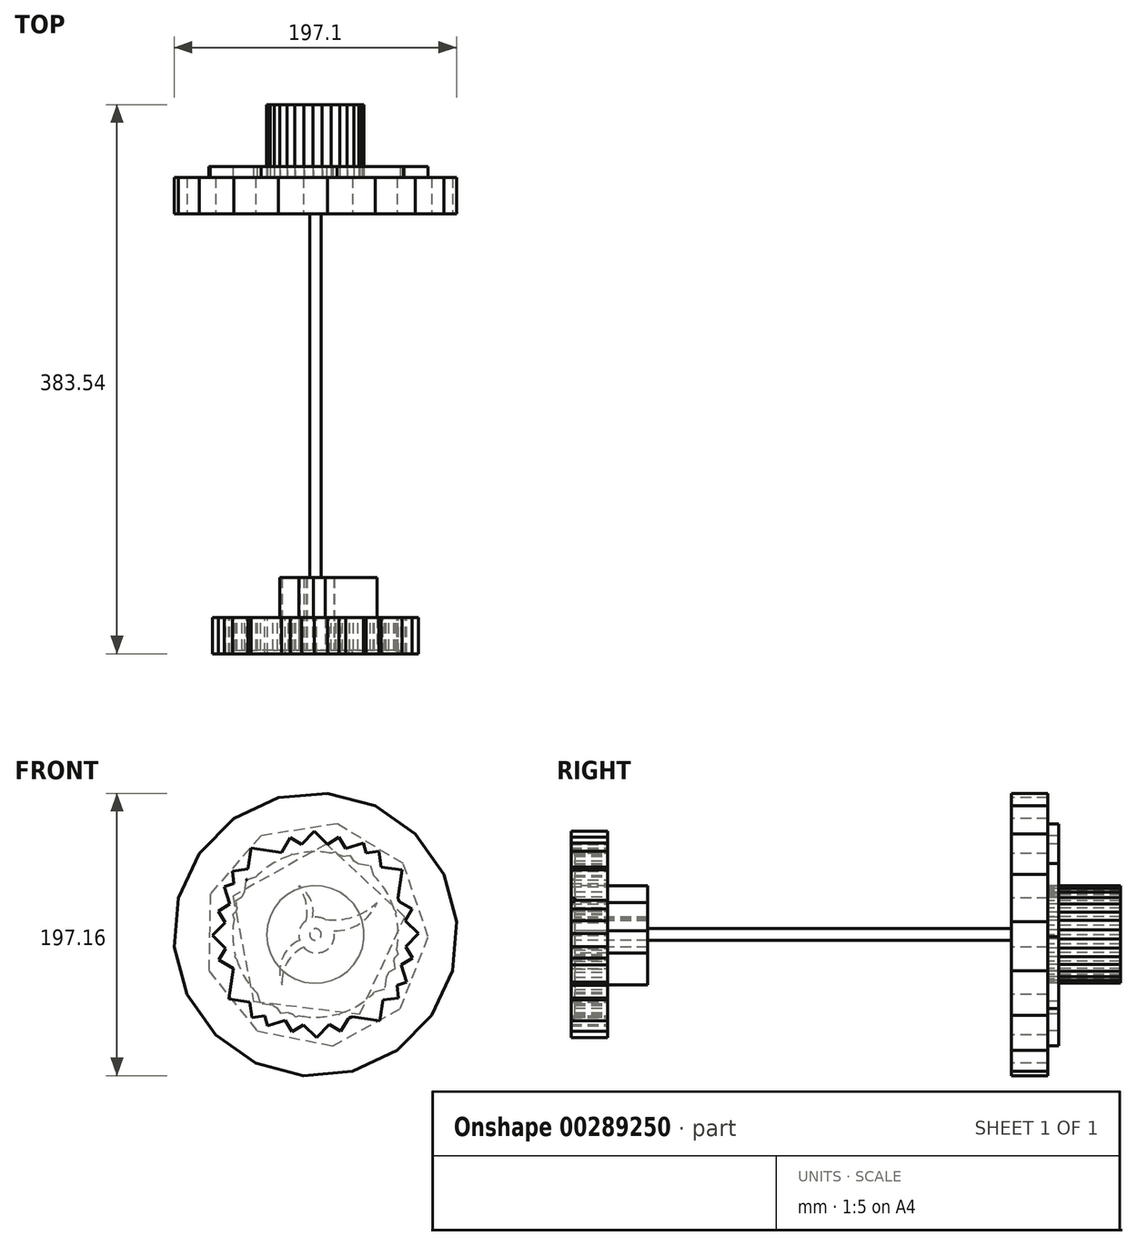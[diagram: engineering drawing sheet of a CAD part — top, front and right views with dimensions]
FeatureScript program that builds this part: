
annotation { "Feature Type Name" : "Feature", "Feature Type Description" : "" }
export const myFeature = defineFeature(function(context is Context, id is Id, definition is map)
    precondition{}
    {
        {
            var Q0;
            Q0=qCreatedBy(makeId("Front.planeOp"),FACE);
            var sketch = newSketch(context, id + "F0", { "sketchPlane" : qUnion([Q0])});
            skCircle(sketch, "E0", {"center": v(0, 0) * mm, "radius": 57.78 * mm});
            skCircle(sketch, "E1.cCircle", {"center": v(0, 0) * mm, "radius": 49.37 * mm, "construction": true});
            skLineSegment(sketch, "E1.0", {"start": v(-67.54, -17.7) * mm, "end": v(-17.7, 67.54) * mm});
            skLineSegment(sketch, "E1.1", {"start": v(-17.7, 67.54) * mm, "end": v(67.54, 17.7) * mm});
            skLineSegment(sketch, "E1.2", {"start": v(67.54, 17.7) * mm, "end": v(17.7, -67.54) * mm});
            skLineSegment(sketch, "E1.3", {"start": v(17.7, -67.54) * mm, "end": v(-67.54, -17.7) * mm});
            skPoint(sketch, "E1.0.midPoint", {"position": v(-42.62, 24.92) * mm});
            skLineSegment(sketch, "E2.0", {"start": v(-67.9, 16.32) * mm, "end": v(16.32, 67.9) * mm});
            skLineSegment(sketch, "E2.1", {"start": v(16.32, 67.9) * mm, "end": v(67.9, -16.32) * mm});
            skLineSegment(sketch, "E2.2", {"start": v(67.9, -16.32) * mm, "end": v(-16.32, -67.9) * mm});
            skLineSegment(sketch, "E2.3", {"start": v(-16.32, -67.9) * mm, "end": v(-67.9, 16.32) * mm});
            skPoint(sketch, "E2.0.midPoint", {"position": v(-25.78, 42.1) * mm});
            skCircle(sketch, "E3.cCircle", {"center": v(0, 0) * mm, "radius": 53.26 * mm, "construction": true});
            skLineSegment(sketch, "E3.0", {"start": v(-45.03, 60.38) * mm, "end": v(60.38, 45.03) * mm});
            skLineSegment(sketch, "E3.1", {"start": v(60.38, 45.03) * mm, "end": v(45.03, -60.38) * mm});
            skLineSegment(sketch, "E3.2", {"start": v(45.03, -60.38) * mm, "end": v(-60.38, -45.03) * mm});
            skLineSegment(sketch, "E3.3", {"start": v(-60.38, -45.03) * mm, "end": v(-45.03, 60.38) * mm});
            skPoint(sketch, "E3.0.midPoint", {"position": v(7.67, 52.7) * mm});
            skCircle(sketch, "E4.cCircle", {"center": v(0, 0) * mm, "radius": 50.9 * mm, "construction": true});
            skLineSegment(sketch, "E4.0", {"start": v(-72, -0.73) * mm, "end": v(-0.73, 72) * mm});
            skLineSegment(sketch, "E4.1", {"start": v(-0.73, 72) * mm, "end": v(72, 0.73) * mm});
            skLineSegment(sketch, "E4.2", {"start": v(72, 0.73) * mm, "end": v(0.73, -72) * mm});
            skLineSegment(sketch, "E4.3", {"start": v(0.73, -72) * mm, "end": v(-72, -0.73) * mm});
            skPoint(sketch, "E4.0.midPoint", {"position": v(-36.36, 35.63) * mm});
            skLineSegment(sketch, "E5.0", {"start": v(-63.79, 33.38) * mm, "end": v(33.38, 63.79) * mm});
            skLineSegment(sketch, "E5.1", {"start": v(33.38, 63.79) * mm, "end": v(63.79, -33.38) * mm});
            skLineSegment(sketch, "E5.2", {"start": v(63.79, -33.38) * mm, "end": v(-33.38, -63.79) * mm});
            skLineSegment(sketch, "E5.3", {"start": v(-33.38, -63.79) * mm, "end": v(-63.79, 33.38) * mm});
            skPoint(sketch, "E5.0.midPoint", {"position": v(-15.2, 48.59) * mm});
            skCircle(sketch, "E6.cCircle", {"center": v(0, 0) * mm, "radius": 51.65 * mm, "construction": true});
            skLineSegment(sketch, "E6.0", {"start": v(-58.08, 44.3) * mm, "end": v(44.3, 58.08) * mm});
            skLineSegment(sketch, "E6.1", {"start": v(44.3, 58.08) * mm, "end": v(58.08, -44.3) * mm});
            skLineSegment(sketch, "E6.2", {"start": v(58.08, -44.3) * mm, "end": v(-44.3, -58.08) * mm});
            skLineSegment(sketch, "E6.3", {"start": v(-44.3, -58.08) * mm, "end": v(-58.08, 44.3) * mm});
            skPoint(sketch, "E6.0.midPoint", {"position": v(-6.9, 51.19) * mm});
            skSolve(sketch);
        }
        {
            var Q0;
            Q0 = qSketchRegion(id + "F0", true);
            extrude(context, id + "F1", {"entities" : qUnion([Q0]), "depth" : 25.4 * mm});
        }
        {
            var Q0;
            Q0=makeQuery(id+"F1.opExtrude","CAP_FACE",FACE,{"disambiguationData":[OSD([sQuery(id+"F0.wireOp",EDGE,"E0"),sQuery(id+"F0.wireOp",EDGE,"E1.0"),sQuery(id+"F0.wireOp",EDGE,"E1.1"),sQuery(id+"F0.wireOp",EDGE,"E1.2"),sQuery(id+"F0.wireOp",EDGE,"E1.3"),sQuery(id+"F0.wireOp",EDGE,"E2.0"),sQuery(id+"F0.wireOp",EDGE,"E2.1"),sQuery(id+"F0.wireOp",EDGE,"E2.2"),sQuery(id+"F0.wireOp",EDGE,"E2.3"),sQuery(id+"F0.wireOp",EDGE,"E3.0"),sQuery(id+"F0.wireOp",EDGE,"E3.1"),sQuery(id+"F0.wireOp",EDGE,"E3.2"),sQuery(id+"F0.wireOp",EDGE,"E3.3"),sQuery(id+"F0.wireOp",EDGE,"E4.0"),sQuery(id+"F0.wireOp",EDGE,"E4.1"),sQuery(id+"F0.wireOp",EDGE,"E4.2"),sQuery(id+"F0.wireOp",EDGE,"E4.3"),sQuery(id+"F0.wireOp",EDGE,"E5.0"),sQuery(id+"F0.wireOp",EDGE,"E5.1"),sQuery(id+"F0.wireOp",EDGE,"E5.2"),sQuery(id+"F0.wireOp",EDGE,"E5.3"),sQuery(id+"F0.wireOp",EDGE,"E6.0"),sQuery(id+"F0.wireOp",EDGE,"E6.1"),sQuery(id+"F0.wireOp",EDGE,"E6.2"),sQuery(id+"F0.wireOp",EDGE,"E6.3")])],"isStart":false});
            var sketch = newSketch(context, id + "F2", { "sketchPlane" : qUnion([Q0])});
            skCircle(sketch, "E7", {"center": v(0.85, -0.42) * mm, "radius": 62.29 * mm});
            skSolve(sketch);
        }
        {
            var Q0;
            Q0 = qSketchRegion(id + "F2", true);
            extrude(context, id + "F3", {"entities" : qUnion([Q0]), "operationType" : NewBodyOperationType.ADD, "oppositeDirection" : true, "depth" : 2.54 * mm});
        }
        {
            var Q0;
            {var subQ1=sQuery(id+"F0.wireOp",EDGE,"E0");var subQ14=sQuery(id+"F0.wireOp",EDGE,"E3.0");var subQ75=makeQuery(id+"F0.imprint","INTERSECT",VERTEX,{"disambiguationData":[OD(0.0)],"derivedFrom":[subQ1,subQ14]});var subQ89=sQuery(id+"F2.wireOp",EDGE,"E7");Q0=makeQuery(id+"F3.boolean.opBoolean","SPLIT",FACE,{"disambiguationData":[TD([makeQuery(id+"F1.opExtrude","SWEPT_FACE",FACE,{"disambiguationData":[OSD([subQ1]),TDD([makeQuery(id+"F0.imprint","IMPRINT",EDGE,{"disambiguationData":[TD([[subQ75,-1.0]])],"derivedFrom":subQ1})])]})])],"derivedFrom":makeQuery(id+"F3.opExtrude","CAP_FACE",FACE,{"disambiguationData":[OSD([subQ89])],"isStart":false})});}
            var sketch = newSketch(context, id + "F4", { "sketchPlane" : qUnion([Q0])});
            skCircle(sketch, "E8", {"center": v(-0.85, -0.42) * mm, "radius": 12.46 * mm});
            skArc(sketch, "E9", {"start": v(-42.97, 22.23) * mm, "mid": v(-31.02, 7.72) * mm, "end": v(-12.93, 2.62) * mm});
            skArc(sketch, "E10", {"start": v(-42.97, 22.23) * mm, "mid": v(-26.23, 12.24) * mm, "end": v(-6.81, 10.52) * mm});
            skArc(sketch, "E11", {"start": v(23.28, -35.14) * mm, "mid": v(23.38, -17.14) * mm, "end": v(11.1, -3.98) * mm});
            skArc(sketch, "E12", {"start": v(23.28, -35.14) * mm, "mid": v(19.84, -19.7) * mm, "end": v(8.2, -9) * mm});
            skArc(sketch, "E13", {"start": v(11.64, 33.87) * mm, "mid": v(3.34, 24.3) * mm, "end": v(1.97, 11.72) * mm});
            skArc(sketch, "E14", {"start": v(11.64, 33.87) * mm, "mid": v(6.6, 22.3) * mm, "end": v(6.46, 9.67) * mm});
            skArc(sketch, "E15", {"start": v(-20.1, -29.85) * mm, "mid": v(-8, -25.09) * mm, "end": v(-3.39, -12.91) * mm});
            skArc(sketch, "E16", {"start": v(-20.1, -29.85) * mm, "mid": v(-12.7, -20.27) * mm, "end": v(-10.44, -8.37) * mm});
            skSolve(sketch);
        }
        {
            var Q0;
            Q0 = qSketchRegion(id + "F4", true);
            extrude(context, id + "F5", {"entities" : qUnion([Q0]), "operationType" : NewBodyOperationType.ADD, "depth" : 50.8 * mm});
        }
        {
            var Q0;
            Q0=makeQuery(id+"F5.opExtrude","CAP_FACE",FACE,{"disambiguationData":[OSD([sQuery(id+"F4.wireOp",EDGE,"E8"),sQuery(id+"F4.wireOp",EDGE,"E9"),sQuery(id+"F4.wireOp",EDGE,"E10"),sQuery(id+"F4.wireOp",EDGE,"E11"),sQuery(id+"F4.wireOp",EDGE,"E12"),sQuery(id+"F4.wireOp",EDGE,"E13"),sQuery(id+"F4.wireOp",EDGE,"E14")])],"isStart":false});
            var sketch = newSketch(context, id + "F6", { "sketchPlane" : qUnion([Q0])});
            skCircle(sketch, "E17", {"center": v(0, 0) * mm, "radius": 4.04 * mm});
            skSolve(sketch);
        }
        {
            var Q0;
            Q0 = qSketchRegion(id + "F6", true);
            extrude(context, id + "F7", {"entities" : qUnion([Q0]), "operationType" : NewBodyOperationType.ADD, "depth" : 254 * mm});
        }
        {
            var Q0;
            Q0=makeQuery(id+"F7.opExtrude","CAP_FACE",FACE,{"disambiguationData":[OSD([sQuery(id+"F6.wireOp",EDGE,"E17")])],"isStart":false});
            var sketch = newSketch(context, id + "F8", { "sketchPlane" : qUnion([Q0])});
            skCircle(sketch, "E18.cCircle", {"center": v(0, 0) * mm, "radius": 97.44 * mm, "construction": true});
            skLineSegment(sketch, "E18.0", {"start": v(-41.64, 89.75) * mm, "end": v(-8.43, 98.58) * mm});
            skLineSegment(sketch, "E18.1", {"start": v(-8.43, 98.58) * mm, "end": v(25.8, 95.52) * mm});
            skLineSegment(sketch, "E18.2", {"start": v(25.8, 95.52) * mm, "end": v(56.9, 80.94) * mm});
            skLineSegment(sketch, "E18.3", {"start": v(56.9, 80.94) * mm, "end": v(81.16, 56.6) * mm});
            skLineSegment(sketch, "E18.4", {"start": v(81.16, 56.6) * mm, "end": v(95.62, 25.42) * mm});
            skLineSegment(sketch, "E18.5", {"start": v(95.62, 25.42) * mm, "end": v(98.55, -8.82) * mm});
            skLineSegment(sketch, "E18.6", {"start": v(98.55, -8.82) * mm, "end": v(89.59, -41.99) * mm});
            skLineSegment(sketch, "E18.7", {"start": v(89.59, -41.99) * mm, "end": v(69.83, -70.1) * mm});
            skLineSegment(sketch, "E18.8", {"start": v(69.83, -70.1) * mm, "end": v(41.64, -89.75) * mm});
            skLineSegment(sketch, "E18.9", {"start": v(41.64, -89.75) * mm, "end": v(8.43, -98.58) * mm});
            skLineSegment(sketch, "E18.10", {"start": v(8.43, -98.58) * mm, "end": v(-25.8, -95.52) * mm});
            skLineSegment(sketch, "E18.11", {"start": v(-25.8, -95.52) * mm, "end": v(-56.9, -80.94) * mm});
            skLineSegment(sketch, "E18.12", {"start": v(-56.9, -80.94) * mm, "end": v(-81.16, -56.6) * mm});
            skLineSegment(sketch, "E18.13", {"start": v(-81.16, -56.6) * mm, "end": v(-95.62, -25.42) * mm});
            skLineSegment(sketch, "E18.14", {"start": v(-95.62, -25.42) * mm, "end": v(-98.55, 8.82) * mm});
            skLineSegment(sketch, "E18.15", {"start": v(-98.55, 8.82) * mm, "end": v(-89.59, 41.99) * mm});
            skLineSegment(sketch, "E18.16", {"start": v(-89.59, 41.99) * mm, "end": v(-69.83, 70.1) * mm});
            skLineSegment(sketch, "E18.17", {"start": v(-69.83, 70.1) * mm, "end": v(-41.64, 89.75) * mm});
            skPoint(sketch, "E18.0.midPoint", {"position": v(-25.04, 94.17) * mm});
            skSolve(sketch);
        }
        {
            var Q0;
            Q0 = qSketchRegion(id + "F8", true);
            extrude(context, id + "F9", {"entities" : qUnion([Q0]), "operationType" : NewBodyOperationType.ADD, "depth" : 25.4 * mm});
        }
        {
            var Q0;
            Q0=makeQuery(id+"F9.opExtrude","CAP_FACE",FACE,{"disambiguationData":[OSD([sQuery(id+"F8.wireOp",EDGE,"E18.0"),sQuery(id+"F8.wireOp",EDGE,"E18.1"),sQuery(id+"F8.wireOp",EDGE,"E18.2"),sQuery(id+"F8.wireOp",EDGE,"E18.3"),sQuery(id+"F8.wireOp",EDGE,"E18.4"),sQuery(id+"F8.wireOp",EDGE,"E18.5"),sQuery(id+"F8.wireOp",EDGE,"E18.6"),sQuery(id+"F8.wireOp",EDGE,"E18.7"),sQuery(id+"F8.wireOp",EDGE,"E18.8"),sQuery(id+"F8.wireOp",EDGE,"E18.9"),sQuery(id+"F8.wireOp",EDGE,"E18.10"),sQuery(id+"F8.wireOp",EDGE,"E18.11"),sQuery(id+"F8.wireOp",EDGE,"E18.12"),sQuery(id+"F8.wireOp",EDGE,"E18.13"),sQuery(id+"F8.wireOp",EDGE,"E18.14"),sQuery(id+"F8.wireOp",EDGE,"E18.15"),sQuery(id+"F8.wireOp",EDGE,"E18.16"),sQuery(id+"F8.wireOp",EDGE,"E18.17")])],"isStart":false});
            var sketch = newSketch(context, id + "F10", { "sketchPlane" : qUnion([Q0])});
            skCircle(sketch, "E19.cCircle", {"center": v(0, 0) * mm, "radius": 74 * mm, "construction": true});
            skLineSegment(sketch, "E19.0", {"start": v(-59.3, -51.8) * mm, "end": v(-78.74, -1.56) * mm});
            skLineSegment(sketch, "E19.1", {"start": v(-78.74, -1.56) * mm, "end": v(-61.32, 49.41) * mm});
            skLineSegment(sketch, "E19.2", {"start": v(-61.32, 49.41) * mm, "end": v(-15.21, 77.27) * mm});
            skLineSegment(sketch, "E19.3", {"start": v(-15.21, 77.27) * mm, "end": v(38.01, 68.97) * mm});
            skLineSegment(sketch, "E19.4", {"start": v(38.01, 68.97) * mm, "end": v(73.45, 28.4) * mm});
            skLineSegment(sketch, "E19.5", {"start": v(73.45, 28.4) * mm, "end": v(74.52, -25.46) * mm});
            skLineSegment(sketch, "E19.6", {"start": v(74.52, -25.46) * mm, "end": v(40.72, -67.4) * mm});
            skLineSegment(sketch, "E19.7", {"start": v(40.72, -67.4) * mm, "end": v(-12.13, -77.81) * mm});
            skLineSegment(sketch, "E19.8", {"start": v(-12.13, -77.81) * mm, "end": v(-59.3, -51.8) * mm});
            skPoint(sketch, "E19.0.midPoint", {"position": v(-69.02, -26.69) * mm});
            skCircle(sketch, "E20.cCircle", {"center": v(0, 0) * mm, "radius": 51.46 * mm, "construction": true});
            skLineSegment(sketch, "E20.0", {"start": v(-30.95, -55.58) * mm, "end": v(-62.42, 12.26) * mm});
            skLineSegment(sketch, "E20.1", {"start": v(-62.42, 12.26) * mm, "end": v(-7.63, 63.15) * mm});
            skLineSegment(sketch, "E20.2", {"start": v(-7.63, 63.15) * mm, "end": v(57.7, 26.77) * mm});
            skLineSegment(sketch, "E20.3", {"start": v(57.7, 26.77) * mm, "end": v(43.3, -46.6) * mm});
            skLineSegment(sketch, "E20.4", {"start": v(43.3, -46.6) * mm, "end": v(-30.95, -55.58) * mm});
            skPoint(sketch, "E20.0.midPoint", {"position": v(-46.68, -21.66) * mm});
            skCircle(sketch, "E21.cCircle", {"center": v(0, 0) * mm, "radius": 20.55 * mm, "construction": true});
            skLineSegment(sketch, "E21.0", {"start": v(-20.55, -35.6) * mm, "end": v(-20.55, 35.6) * mm});
            skLineSegment(sketch, "E21.1", {"start": v(-20.55, 35.6) * mm, "end": v(41.1, 0) * mm});
            skLineSegment(sketch, "E21.2", {"start": v(41.1, 0) * mm, "end": v(-20.55, -35.6) * mm});
            skPoint(sketch, "E21.0.midPoint", {"position": v(-20.55, 0) * mm});
            skCircle(sketch, "E22.cCircle", {"center": v(0, 0) * mm, "radius": 7.21 * mm, "construction": true});
            skLineSegment(sketch, "E22.0", {"start": v(-7.21, -1.43) * mm, "end": v(-7.21, 1.43) * mm});
            skLineSegment(sketch, "E22.1", {"start": v(-7.21, 1.43) * mm, "end": v(-6.11, 4.08) * mm});
            skLineSegment(sketch, "E22.2", {"start": v(-6.11, 4.08) * mm, "end": v(-4.08, 6.11) * mm});
            skLineSegment(sketch, "E22.3", {"start": v(-4.08, 6.11) * mm, "end": v(-1.43, 7.21) * mm});
            skLineSegment(sketch, "E22.4", {"start": v(-1.43, 7.21) * mm, "end": v(1.43, 7.21) * mm});
            skLineSegment(sketch, "E22.5", {"start": v(1.43, 7.21) * mm, "end": v(4.08, 6.11) * mm});
            skLineSegment(sketch, "E22.6", {"start": v(4.08, 6.11) * mm, "end": v(6.11, 4.08) * mm});
            skLineSegment(sketch, "E22.7", {"start": v(6.11, 4.08) * mm, "end": v(7.21, 1.43) * mm});
            skLineSegment(sketch, "E22.8", {"start": v(7.21, 1.43) * mm, "end": v(7.21, -1.43) * mm});
            skLineSegment(sketch, "E22.9", {"start": v(7.21, -1.43) * mm, "end": v(6.11, -4.08) * mm});
            skLineSegment(sketch, "E22.10", {"start": v(6.11, -4.08) * mm, "end": v(4.08, -6.11) * mm});
            skLineSegment(sketch, "E22.11", {"start": v(4.08, -6.11) * mm, "end": v(1.43, -7.21) * mm});
            skLineSegment(sketch, "E22.12", {"start": v(1.43, -7.21) * mm, "end": v(-1.43, -7.21) * mm});
            skLineSegment(sketch, "E22.13", {"start": v(-1.43, -7.21) * mm, "end": v(-4.08, -6.11) * mm});
            skLineSegment(sketch, "E22.14", {"start": v(-4.08, -6.11) * mm, "end": v(-6.11, -4.08) * mm});
            skLineSegment(sketch, "E22.15", {"start": v(-6.11, -4.08) * mm, "end": v(-7.21, -1.43) * mm});
            skPoint(sketch, "E22.0.midPoint", {"position": v(-7.21, 0) * mm});
            skSolve(sketch);
        }
        {
            var Q0;
            Q0 = qSketchRegion(id + "F10", true);
            extrude(context, id + "F11", {"entities" : qUnion([Q0]), "operationType" : NewBodyOperationType.ADD, "depth" : 7.62 * mm});
        }
        {
            var Q0;
            Q0=makeQuery(id+"F11.boolean.opBoolean","SPLIT",FACE,{"disambiguationData":[TD([makeQuery(id+"F11.opExtrude","SWEPT_FACE",FACE,{"disambiguationData":[OSD([sQuery(id+"F10.wireOp",EDGE,"E20.0")])]})])],"derivedFrom":makeQuery(id+"F9.opExtrude","CAP_FACE",FACE,{"disambiguationData":[OSD([sQuery(id+"F8.wireOp",EDGE,"E18.0"),sQuery(id+"F8.wireOp",EDGE,"E18.1"),sQuery(id+"F8.wireOp",EDGE,"E18.2"),sQuery(id+"F8.wireOp",EDGE,"E18.3"),sQuery(id+"F8.wireOp",EDGE,"E18.4"),sQuery(id+"F8.wireOp",EDGE,"E18.5"),sQuery(id+"F8.wireOp",EDGE,"E18.6"),sQuery(id+"F8.wireOp",EDGE,"E18.7"),sQuery(id+"F8.wireOp",EDGE,"E18.8"),sQuery(id+"F8.wireOp",EDGE,"E18.9"),sQuery(id+"F8.wireOp",EDGE,"E18.10"),sQuery(id+"F8.wireOp",EDGE,"E18.11"),sQuery(id+"F8.wireOp",EDGE,"E18.12"),sQuery(id+"F8.wireOp",EDGE,"E18.13"),sQuery(id+"F8.wireOp",EDGE,"E18.14"),sQuery(id+"F8.wireOp",EDGE,"E18.15"),sQuery(id+"F8.wireOp",EDGE,"E18.16"),sQuery(id+"F8.wireOp",EDGE,"E18.17")])],"isStart":false})});
            var sketch = newSketch(context, id + "F12", { "sketchPlane" : qUnion([Q0])});
            skCircle(sketch, "E23.cCircle", {"center": v(0, 0) * mm, "radius": 33.93 * mm, "construction": true});
            skLineSegment(sketch, "E23.0", {"start": v(-30.36, -15.5) * mm, "end": v(-32.74, -9.48) * mm});
            skLineSegment(sketch, "E23.1", {"start": v(-32.74, -9.48) * mm, "end": v(-33.94, -3.1) * mm});
            skLineSegment(sketch, "E23.2", {"start": v(-33.94, -3.1) * mm, "end": v(-33.92, 3.37) * mm});
            skLineSegment(sketch, "E23.3", {"start": v(-33.92, 3.37) * mm, "end": v(-32.67, 9.73) * mm});
            skLineSegment(sketch, "E23.4", {"start": v(-32.67, 9.73) * mm, "end": v(-30.24, 15.74) * mm});
            skLineSegment(sketch, "E23.5", {"start": v(-30.24, 15.74) * mm, "end": v(-26.71, 21.18) * mm});
            skLineSegment(sketch, "E23.6", {"start": v(-26.71, 21.18) * mm, "end": v(-22.22, 25.85) * mm});
            skLineSegment(sketch, "E23.7", {"start": v(-22.22, 25.85) * mm, "end": v(-16.93, 29.59) * mm});
            skLineSegment(sketch, "E23.8", {"start": v(-16.93, 29.59) * mm, "end": v(-11.02, 32.26) * mm});
            skLineSegment(sketch, "E23.9", {"start": v(-11.02, 32.26) * mm, "end": v(-4.72, 33.76) * mm});
            skLineSegment(sketch, "E23.10", {"start": v(-4.72, 33.76) * mm, "end": v(1.75, 34.04) * mm});
            skLineSegment(sketch, "E23.11", {"start": v(1.75, 34.04) * mm, "end": v(8.17, 33.1) * mm});
            skLineSegment(sketch, "E23.12", {"start": v(8.17, 33.1) * mm, "end": v(14.28, 30.95) * mm});
            skLineSegment(sketch, "E23.13", {"start": v(14.28, 30.95) * mm, "end": v(19.88, 27.69) * mm});
            skLineSegment(sketch, "E23.14", {"start": v(19.88, 27.69) * mm, "end": v(24.76, 23.43) * mm});
            skLineSegment(sketch, "E23.15", {"start": v(24.76, 23.43) * mm, "end": v(28.75, 18.32) * mm});
            skLineSegment(sketch, "E23.16", {"start": v(28.75, 18.32) * mm, "end": v(31.7, 12.55) * mm});
            skLineSegment(sketch, "E23.17", {"start": v(31.7, 12.55) * mm, "end": v(33.5, 6.32) * mm});
            skLineSegment(sketch, "E23.18", {"start": v(33.5, 6.32) * mm, "end": v(34.09, -0.13) * mm});
            skLineSegment(sketch, "E23.19", {"start": v(34.09, -0.13) * mm, "end": v(33.45, -6.58) * mm});
            skLineSegment(sketch, "E23.20", {"start": v(33.45, -6.58) * mm, "end": v(31.6, -12.8) * mm});
            skLineSegment(sketch, "E23.21", {"start": v(31.6, -12.8) * mm, "end": v(28.6, -18.54) * mm});
            skLineSegment(sketch, "E23.22", {"start": v(28.6, -18.54) * mm, "end": v(24.58, -23.62) * mm});
            skLineSegment(sketch, "E23.23", {"start": v(24.58, -23.62) * mm, "end": v(19.66, -27.84) * mm});
            skLineSegment(sketch, "E23.24", {"start": v(19.66, -27.84) * mm, "end": v(14.04, -31.06) * mm});
            skLineSegment(sketch, "E23.25", {"start": v(14.04, -31.06) * mm, "end": v(7.9, -33.16) * mm});
            skLineSegment(sketch, "E23.26", {"start": v(7.9, -33.16) * mm, "end": v(1.49, -34.05) * mm});
            skLineSegment(sketch, "E23.27", {"start": v(1.49, -34.05) * mm, "end": v(-4.98, -33.72) * mm});
            skLineSegment(sketch, "E23.28", {"start": v(-4.98, -33.72) * mm, "end": v(-11.27, -32.17) * mm});
            skLineSegment(sketch, "E23.29", {"start": v(-11.27, -32.17) * mm, "end": v(-17.16, -29.45) * mm});
            skLineSegment(sketch, "E23.30", {"start": v(-17.16, -29.45) * mm, "end": v(-22.42, -25.67) * mm});
            skLineSegment(sketch, "E23.31", {"start": v(-22.42, -25.67) * mm, "end": v(-26.88, -20.97) * mm});
            skLineSegment(sketch, "E23.32", {"start": v(-26.88, -20.97) * mm, "end": v(-30.36, -15.5) * mm});
            skPoint(sketch, "E23.0.midPoint", {"position": v(-31.55, -12.49) * mm});
            skSolve(sketch);
        }
        {
            var Q0;
            Q0 = qSketchRegion(id + "F12", true);
            extrude(context, id + "F13", {"entities" : qUnion([Q0]), "operationType" : NewBodyOperationType.ADD, "depth" : 50.8 * mm});
        }
    });
